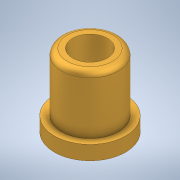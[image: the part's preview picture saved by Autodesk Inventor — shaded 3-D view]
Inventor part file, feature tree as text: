
AUTODESK INVENTOR PART (.ipt)
format: ipt  version: 2022 (Build 260153000, 153)  size: 135,168 bytes
history: native  units: mm
features: extrude x3, sketch x3, fillet x1
ambient origin geometry x8: Origin, YZ Plane, XZ Plane, XY Plane, X Axis, Y Axis, Z Axis, Center Point
bodies: Solid1 (feature_tree)
feature tree (7):
  extrude  "Extrusion1"  Depth=25.5mm TaperAngle=0.0deg
  extrude  "Extrusion2"  TaperAngle=0.0deg  [1 undecoded]
  extrude  "Extrusion3"  Depth=5.0mm TaperAngle=0.0deg
  fillet  "Fillet1"  Radius=2.0mm
  sketch  "Sketch1"  dims[d0=20.0mm d1=25.5mm d2=0.0mm]
  sketch  "Sketch2"  dims[d3=12.2mm d4=0.0mm d5=0.0mm]
  sketch  "Sketch3"  dims[d6=25.0mm d7=5.0mm d8=0.0mm d9=2.0mm]
note: 1 required parameter value undecoded (feature->parameter linkage not recoverable at this tier; creation-order binding heuristic only, values carry confidence <= 0.55)
